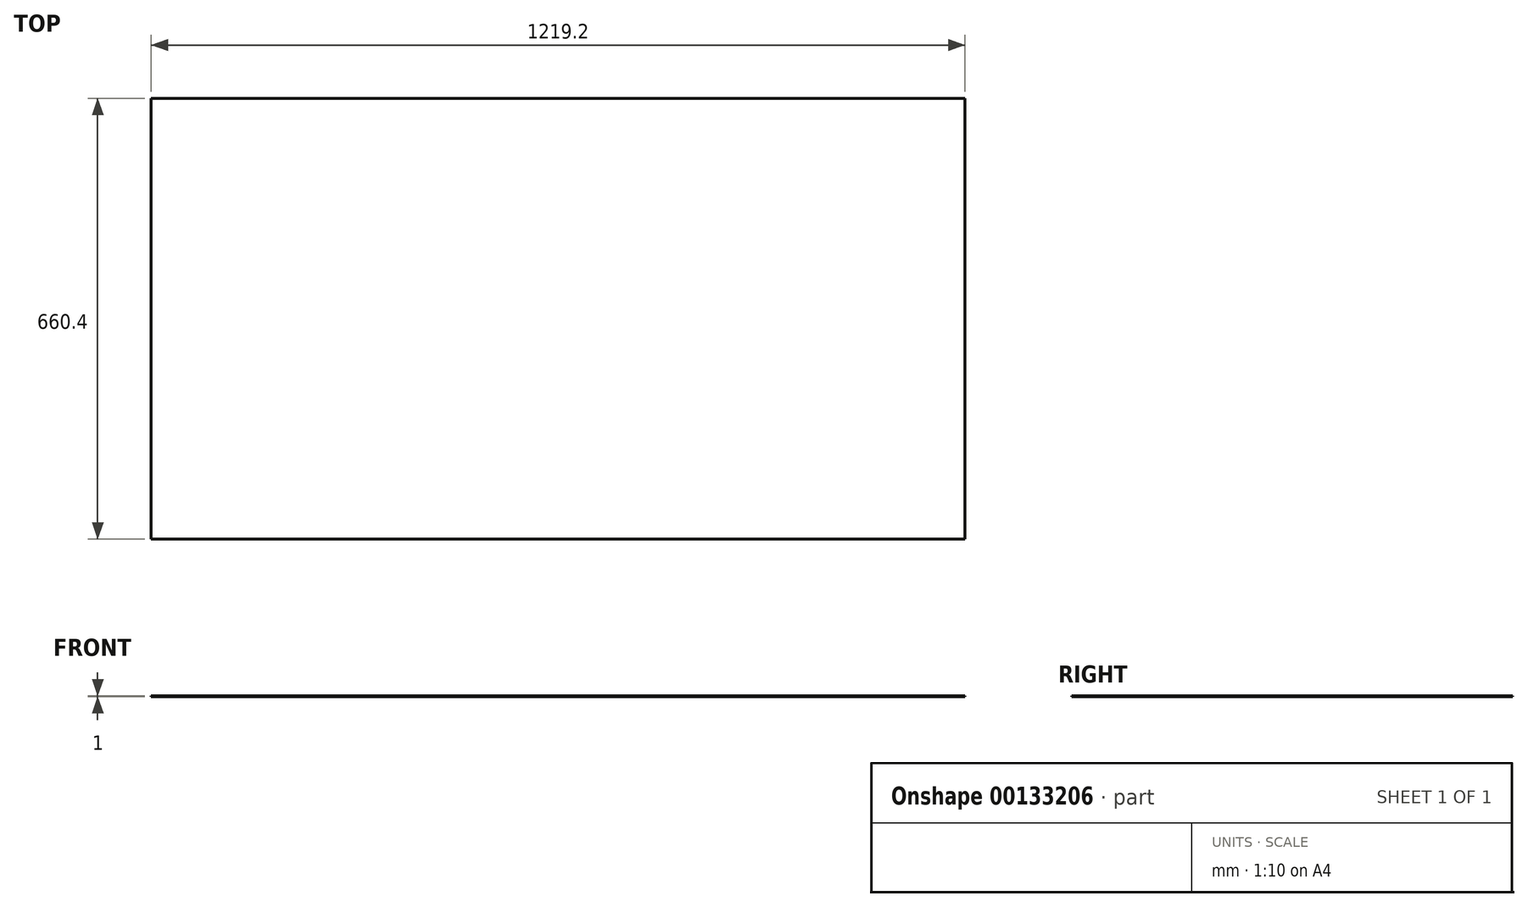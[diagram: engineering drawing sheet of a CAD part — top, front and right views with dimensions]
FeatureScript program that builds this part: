
annotation { "Feature Type Name" : "Feature", "Feature Type Description" : "" }
export const myFeature = defineFeature(function(context is Context, id is Id, definition is map)
    precondition{}
    {
        {
            var Q0;
            Q0=qCreatedBy(makeId("Top.planeOp"),FACE);
            var sketch = newSketch(context, id + "F0", { "sketchPlane" : qUnion([Q0])});
            skLineSegment(sketch, "E0.bottom", {"start": v(0, 660.4) * mm, "end": v(1219.2, 660.4) * mm});
            skLineSegment(sketch, "E0.top", {"start": v(0, 0) * mm, "end": v(1219.2, 0) * mm});
            skLineSegment(sketch, "E0.left", {"start": v(0, 660.4) * mm, "end": v(0, 0) * mm});
            skLineSegment(sketch, "E0.right", {"start": v(1219.2, 660.4) * mm, "end": v(1219.2, 0) * mm});
            skSolve(sketch);
        }
        {
            var Q0;
            Q0 = qSketchRegion(id + "F0", true);
            extrude(context, id + "F1", {"entities" : qUnion([Q0]), "depth" : 1 * mm, "offsetDistance" : 25 * mm});
        }
    });
